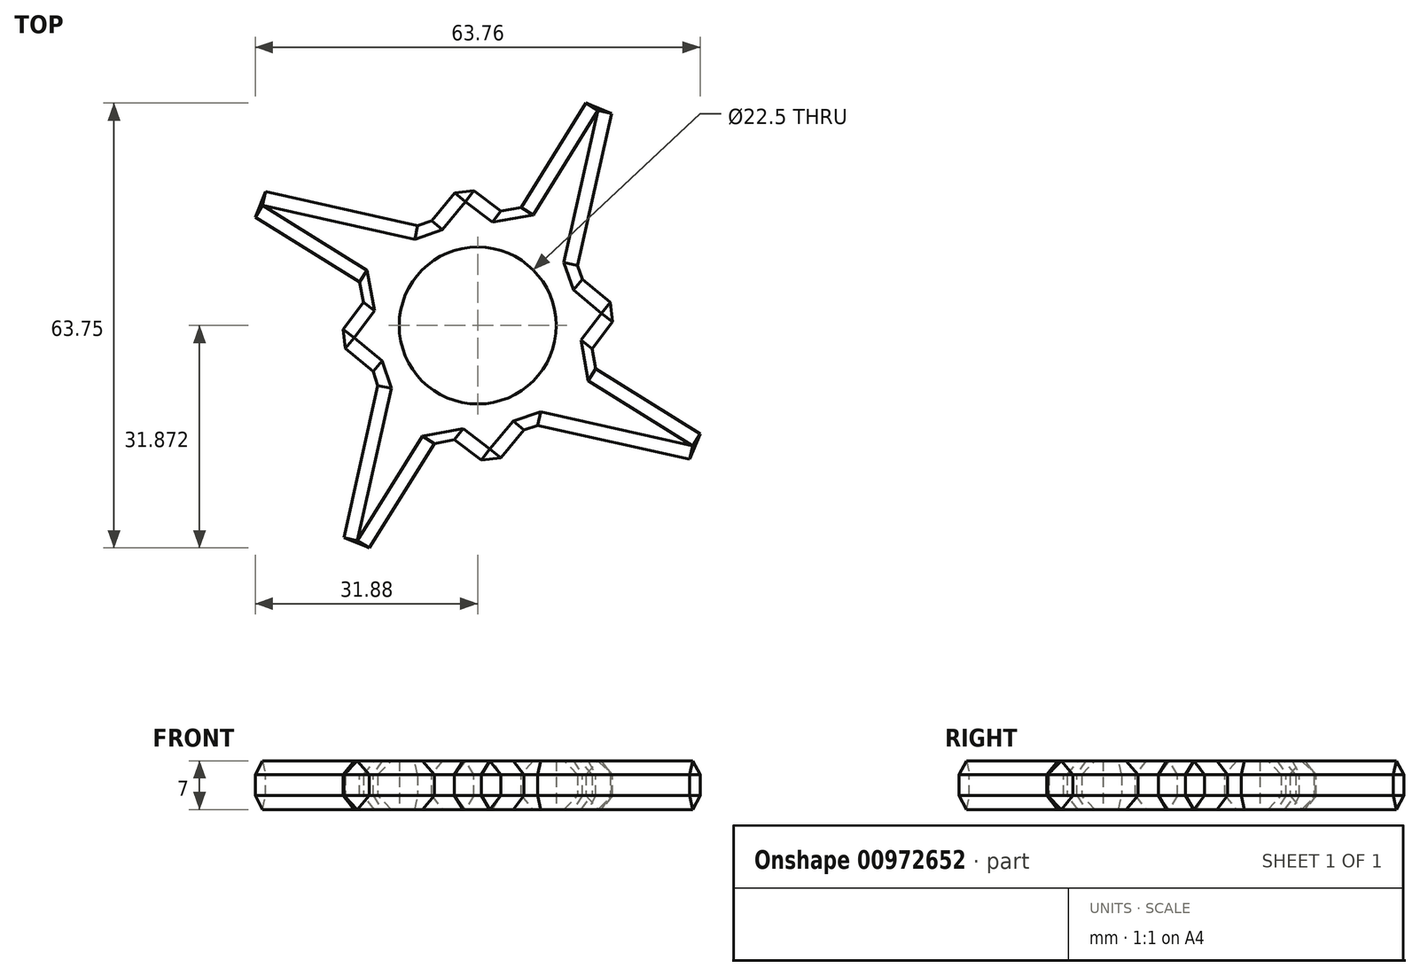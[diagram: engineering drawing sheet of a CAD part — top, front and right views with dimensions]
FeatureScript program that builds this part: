
annotation { "Feature Type Name" : "Feature", "Feature Type Description" : "" }
export const myFeature = defineFeature(function(context is Context, id is Id, definition is map)
    precondition{}
    {
        {
            var Q0;
            Q0=qCreatedBy(makeId("Top.planeOp"),FACE);
            var sketch = newSketch(context, id + "F0", { "sketchPlane" : qUnion([Q0])});
            skCircle(sketch, "E0", {"center": v(-59.14, 9.6) * mm, "radius": 11.25 * mm});
            skCircle(sketch, "E1", {"center": v(-59.14, 9.6) * mm, "radius": 15.88 * mm});
            skLineSegment(sketch, "E2", {"start": v(-66.53, 23.64) * mm, "end": v(-61.22, 30.07) * mm});
            skLineSegment(sketch, "E3", {"start": v(-61.22, 30.07) * mm, "end": v(-54.08, 24.64) * mm});
            skLineSegment(sketch, "E4.1.0", {"start": v(-73.19, 2.2) * mm, "end": v(-79.62, 7.51) * mm});
            skLineSegment(sketch, "E4.1.1", {"start": v(-79.62, 7.51) * mm, "end": v(-74.19, 14.66) * mm});
            skLineSegment(sketch, "E4.2.0", {"start": v(-51.75, -4.46) * mm, "end": v(-57.06, -10.89) * mm});
            skLineSegment(sketch, "E4.2.1", {"start": v(-57.06, -10.89) * mm, "end": v(-64.2, -5.45) * mm});
            skLineSegment(sketch, "E4.3.0", {"start": v(-45.1, 16.98) * mm, "end": v(-38.66, 11.67) * mm});
            skLineSegment(sketch, "E4.3.1", {"start": v(-38.66, 11.67) * mm, "end": v(-44.1, 4.53) * mm});
            skLineSegment(sketch, "E5", {"start": v(-51.75, -4.46) * mm, "end": v(-17.27, -12.15) * mm});
            skLineSegment(sketch, "E6", {"start": v(-17.27, -12.15) * mm, "end": v(-44.1, 4.53) * mm});
            skLineSegment(sketch, "E7.1.0", {"start": v(-45.1, 16.98) * mm, "end": v(-37.4, 51.46) * mm});
            skLineSegment(sketch, "E7.1.1", {"start": v(-37.4, 51.46) * mm, "end": v(-54.08, 24.64) * mm});
            skLineSegment(sketch, "E7.2.0", {"start": v(-66.53, 23.64) * mm, "end": v(-101, 31.34) * mm});
            skLineSegment(sketch, "E7.2.1", {"start": v(-101, 31.34) * mm, "end": v(-74.19, 14.66) * mm});
            skLineSegment(sketch, "E7.3.0", {"start": v(-73.19, 2.2) * mm, "end": v(-80.88, -32.28) * mm});
            skLineSegment(sketch, "E7.3.1", {"start": v(-80.88, -32.28) * mm, "end": v(-64.2, -5.45) * mm});
            skSolve(sketch);
        }
        {
            var Q0;
            Q0 = qSketchRegion(id + "F0", true);
            extrude(context, id + "F1", {"entities" : qUnion([Q0]), "depth" : 7 * mm, "offsetDistance" : 25 * mm});
        }
        {
            var Q0;
            Q0=makeQuery(id+"F1.opExtrude","CAP_EDGE",EDGE,{"disambiguationData":[OSD([sQuery(id+"F0.wireOp",EDGE,"E7.3.0")])],"isStart":true});
            var Q1;
            Q1=makeQuery(id+"F1.opExtrude","SWEPT_FACE",FACE,{"disambiguationData":[OSD([sQuery(id+"F0.wireOp",EDGE,"E7.3.0")])]});
            var Q2;
            Q2=makeQuery(id+"F1.opExtrude","SWEPT_FACE",FACE,{"disambiguationData":[OSD([sQuery(id+"F0.wireOp",EDGE,"E4.1.1")])]});
            var Q3;
            Q3=makeQuery(id+"F1.opExtrude","SWEPT_FACE",FACE,{"disambiguationData":[OSD([sQuery(id+"F0.wireOp",EDGE,"E7.2.0")])]});
            var Q4;
            Q4=makeQuery(id+"F1.opExtrude","SWEPT_FACE",FACE,{"disambiguationData":[OSD([sQuery(id+"F0.wireOp",EDGE,"E7.1.1")])]});
            var Q5;
            Q5=makeQuery(id+"F1.opExtrude","SWEPT_FACE",FACE,{"disambiguationData":[OSD([sQuery(id+"F0.wireOp",EDGE,"E7.1.0")])]});
            var Q6;
            Q6=makeQuery(id+"F1.opExtrude","SWEPT_FACE",FACE,{"disambiguationData":[OSD([sQuery(id+"F0.wireOp",EDGE,"E6")])]});
            var Q7;
            Q7=makeQuery(id+"F1.opExtrude","SWEPT_FACE",FACE,{"disambiguationData":[OSD([sQuery(id+"F0.wireOp",EDGE,"E5")])]});
            var Q8;
            Q8=makeQuery(id+"F1.opExtrude","SWEPT_FACE",FACE,{"disambiguationData":[OSD([sQuery(id+"F0.wireOp",EDGE,"E7.3.1")])]});
            var Q9;
            Q9=makeQuery(id+"F1.opExtrude","SWEPT_EDGE",EDGE,{"disambiguationData":[OSD([sQuery(id+"F0.wireOp",EDGE,"E4.2.0"),sQuery(id+"F0.wireOp",EDGE,"E4.2.1")])]});
            var Q10;
            Q10=makeQuery(id+"F1.opExtrude","SWEPT_EDGE",EDGE,{"disambiguationData":[OSD([sQuery(id+"F0.wireOp",EDGE,"E4.3.0"),sQuery(id+"F0.wireOp",EDGE,"E4.3.1")])]});
            var Q11;
            Q11=makeQuery(id+"F1.opExtrude","SWEPT_EDGE",EDGE,{"disambiguationData":[OSD([sQuery(id+"F0.wireOp",EDGE,"E2"),sQuery(id+"F0.wireOp",EDGE,"E3")])]});
            chamfer(context, id + "F2", {"entities" : qUnion([Q0, Q1, Q2, Q3, Q4, Q5, Q6, Q7, Q8, Q9, Q10, Q11]), "width" : 2 * mm, "tangentPropagation" : true});
        }
    });
